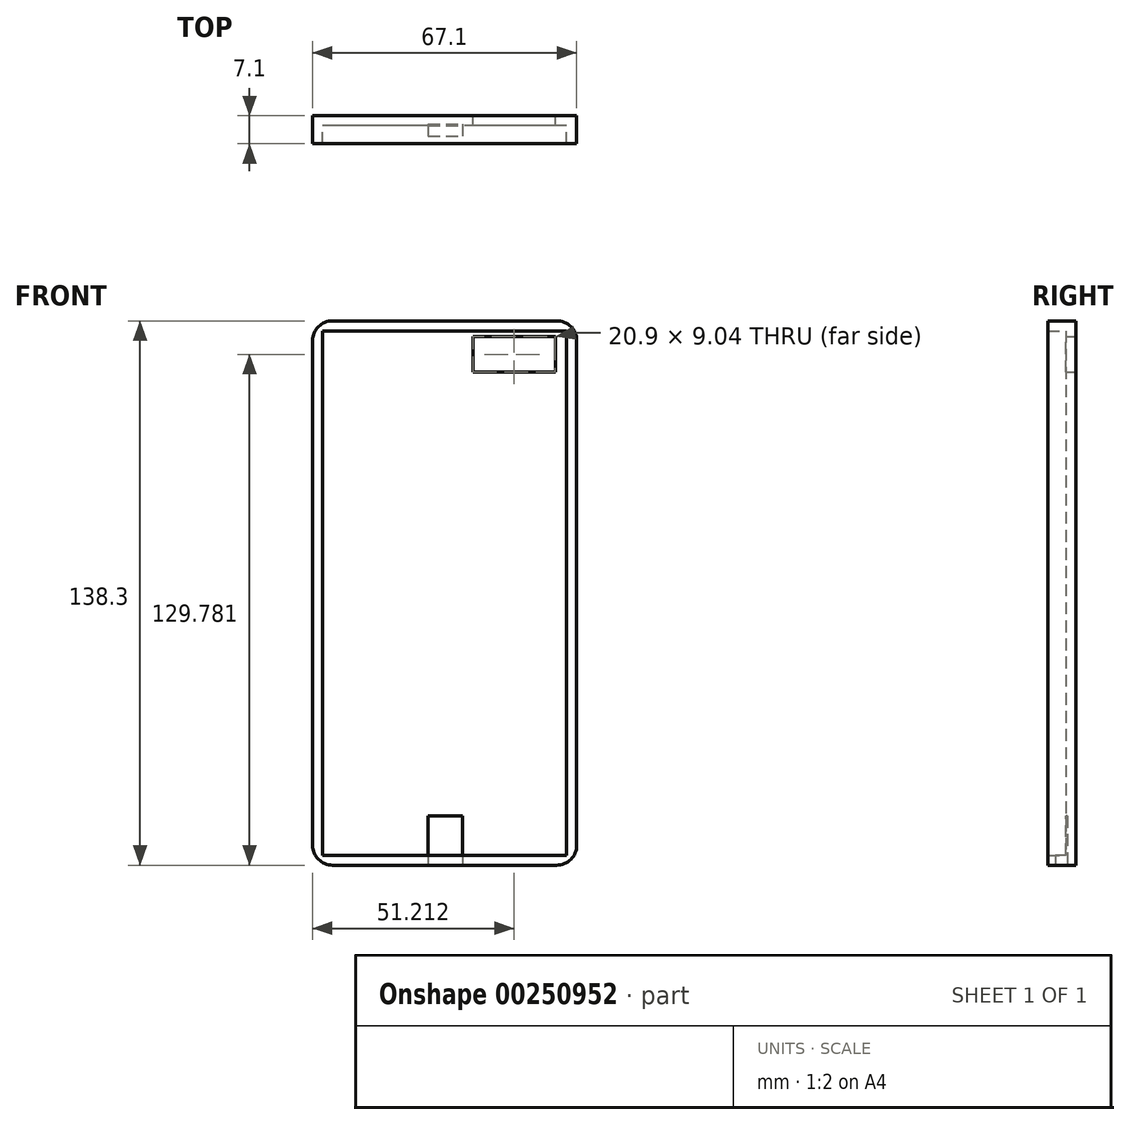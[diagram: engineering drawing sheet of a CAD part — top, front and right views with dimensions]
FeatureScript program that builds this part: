
annotation { "Feature Type Name" : "Feature", "Feature Type Description" : "" }
export const myFeature = defineFeature(function(context is Context, id is Id, definition is map)
    precondition{}
    {
        {
            var Q0;
            Q0=qCreatedBy(makeId("Front.planeOp"),FACE);
            var sketch = newSketch(context, id + "F0", { "sketchPlane" : qUnion([Q0])});
            skLineSegment(sketch, "E0.bottom", {"start": v(33.55, 69.15) * mm, "end": v(-33.55, 69.15) * mm});
            skLineSegment(sketch, "E0.top", {"start": v(33.55, -69.15) * mm, "end": v(-33.55, -69.15) * mm});
            skLineSegment(sketch, "E0.left", {"start": v(33.55, 69.15) * mm, "end": v(33.55, -69.15) * mm});
            skLineSegment(sketch, "E0.right", {"start": v(-33.55, 69.15) * mm, "end": v(-33.55, -69.15) * mm});
            skPoint(sketch, "E0.middle", {"position": v(0, 0) * mm});
            skSolve(sketch);
        }
        {
            var Q0;
            Q0=makeQuery(id+"F0.imprint","IMPRINT",FACE,{"disambiguationData":[TD([[makeQuery(id+"F0.imprint","IMPRINT",EDGE,{"derivedFrom":sQuery(id+"F0.wireOp",EDGE,"E0.bottom")}),1.0]])]});
            extrude(context, id + "F1", {"entities" : qUnion([Q0]), "endBound" : BoundingType.SYMMETRIC, "depth" : 7.1 * mm});
        }
        {
            var Q0;
            Q0=makeQuery(id+"F1.opExtrude","CAP_FACE",FACE,{"disambiguationData":[OSD([sQuery(id+"F0.wireOp",EDGE,"E0.bottom"),sQuery(id+"F0.wireOp",EDGE,"E0.top"),sQuery(id+"F0.wireOp",EDGE,"E0.left"),sQuery(id+"F0.wireOp",EDGE,"E0.right")])],"isStart":false});
            shell(context, id + "F2", {"entities" : qUnion([Q0]), "thickness" : 2.54 * mm});
        }
        {
            var Q0;
            Q0=makeQuery(id+"F1.opExtrude","SWEPT_EDGE",EDGE,{"disambiguationData":[OSD([sQuery(id+"F0.wireOp",EDGE,"E0.top"),sQuery(id+"F0.wireOp",EDGE,"E0.right")])]});
            var Q1;
            Q1=makeQuery(id+"F1.opExtrude","SWEPT_EDGE",EDGE,{"disambiguationData":[OSD([sQuery(id+"F0.wireOp",EDGE,"E0.bottom"),sQuery(id+"F0.wireOp",EDGE,"E0.right")])]});
            var Q2;
            Q2=makeQuery(id+"F1.opExtrude","SWEPT_EDGE",EDGE,{"disambiguationData":[OSD([sQuery(id+"F0.wireOp",EDGE,"E0.bottom"),sQuery(id+"F0.wireOp",EDGE,"E0.left")])]});
            var Q3;
            Q3=makeQuery(id+"F1.opExtrude","SWEPT_EDGE",EDGE,{"disambiguationData":[OSD([sQuery(id+"F0.wireOp",EDGE,"E0.top"),sQuery(id+"F0.wireOp",EDGE,"E0.left")])]});
            fillet(context, id + "F3", {"entities" : qUnion([Q0, Q1, Q2, Q3]), "radius" : 5.08 * mm, "tangentPropagation" : true, "allowEdgeOverflow" : false});
        }
        {
            var Q0;
            Q0=qCreatedBy(makeId("Front.planeOp"),FACE);
            var sketch = newSketch(context, id + "F4", { "sketchPlane" : qUnion([Q0])});
            skLineSegment(sketch, "E1.bottom", {"start": v(7.21, 65.15) * mm, "end": v(28.1, 65.15) * mm});
            skLineSegment(sketch, "E1.top", {"start": v(7.21, 56.11) * mm, "end": v(28.1, 56.11) * mm});
            skLineSegment(sketch, "E1.left", {"start": v(7.21, 65.15) * mm, "end": v(7.21, 56.11) * mm});
            skLineSegment(sketch, "E1.right", {"start": v(28.1, 65.15) * mm, "end": v(28.1, 56.11) * mm});
            skSolve(sketch);
        }
        {
            var Q0;
            Q0=makeQuery(id+"F4.imprint","IMPRINT",FACE,{"disambiguationData":[TD([[makeQuery(id+"F4.imprint","IMPRINT",EDGE,{"derivedFrom":sQuery(id+"F4.wireOp",EDGE,"E1.bottom")}),-1.0]])]});
            extrude(context, id + "F5", {"entities" : qUnion([Q0]), "operationType" : NewBodyOperationType.REMOVE, "endBound" : BoundingType.SYMMETRIC, "depth" : 25 * mm});
        }
        {
            var Q0;
            Q0=makeQuery(id+"F1.opExtrude","SWEPT_FACE",FACE,{"disambiguationData":[OSD([sQuery(id+"F0.wireOp",EDGE,"E0.top")])]});
            var sketch = newSketch(context, id + "F6", { "sketchPlane" : qUnion([Q0])});
            skLineSegment(sketch, "E2.bottom", {"start": v(-4.2, -1.5) * mm, "end": v(4.59, -1.5) * mm});
            skLineSegment(sketch, "E2.top", {"start": v(-4.2, 1.64) * mm, "end": v(4.59, 1.64) * mm});
            skLineSegment(sketch, "E2.left", {"start": v(-4.2, -1.5) * mm, "end": v(-4.2, 1.64) * mm});
            skLineSegment(sketch, "E2.right", {"start": v(4.59, -1.5) * mm, "end": v(4.59, 1.64) * mm});
            skSolve(sketch);
        }
        {
            var Q0;
            Q0=makeQuery(id+"F6.imprint","IMPRINT",FACE,{"disambiguationData":[TD([[makeQuery(id+"F6.imprint","IMPRINT",EDGE,{"derivedFrom":sQuery(id+"F6.wireOp",EDGE,"E2.bottom")}),1.0]])]});
            extrude(context, id + "F7", {"entities" : qUnion([Q0]), "operationType" : NewBodyOperationType.REMOVE, "endBound" : BoundingType.SYMMETRIC, "oppositeDirection" : true, "depth" : 25 * mm});
        }
    });
